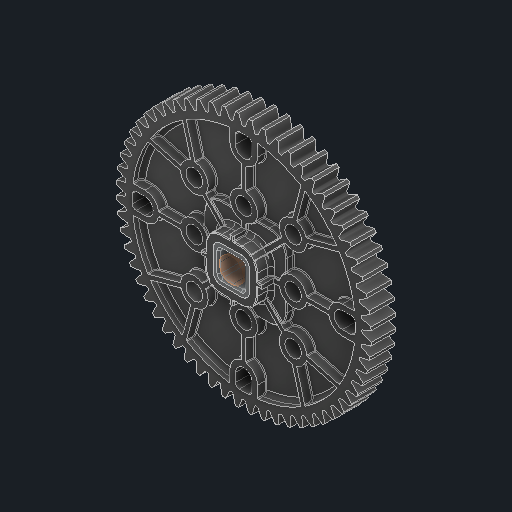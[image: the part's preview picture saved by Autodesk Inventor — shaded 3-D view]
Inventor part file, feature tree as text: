
AUTODESK INVENTOR PART (.ipt)
format: ipt  version: 2025 (Build 290162000, 162)  size: 3,913,728 bytes
history: native  units: in
note: dims shown in document units (in); Inventor stores cm internally (conversion verified against a paired STEP export)
features: other x3, extrude x3, sketch x2
ambient origin geometry x8: Origin, YZ Plane, XZ Plane, XY Plane, X Axis, Y Axis, Z Axis, Center Point
bodies: Solid1 (feature_tree), Solid2 (feature_tree)
feature tree (8):
  other  "276-7748-001_OVERMOLD Rev3_60T 24DP Gear Rev1_1:1"
  extrude  "Extrusion1"  Depth=0.3937in TaperAngle=0.0deg
  extrude  "Extrusion2"  Depth=0.125in TaperAngle=0.0deg
  other  "Srf1"
  sketch  "Sketch2"  dims[d0=0.25in d1=0.3937in d2=0.0in]
  sketch  "Sketch3"  dims[d3=0.125in d4=0.0in d5=0.125in d6=0.0in]
  other  "276-7573-002 Rev7_2:1"
  extrude  "ExtrusionSrf1"  [1 undecoded]
note: 1 required parameter value undecoded (feature->parameter linkage not recoverable at this tier; creation-order binding heuristic only, values carry confidence <= 0.55)
